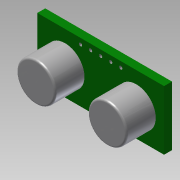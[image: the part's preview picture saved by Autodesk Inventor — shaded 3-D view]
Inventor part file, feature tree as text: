
AUTODESK INVENTOR PART (.ipt)
format: ipt  version: 2015 SP1 (Build 190203100, 203)  size: 141,824 bytes
history: native  units: mm
features: extrude x3, sketch x2, fillet x1, projected_geometry x1
ambient origin geometry x8: Origin, YZ Plane, XZ Plane, XY Plane, X Axis, Y Axis, Z Axis, Center Point
bodies: Solid1 (feature_tree)
feature tree (7):
  extrude  "Extrusion1"  Depth=15.0mm
  sketch  "Sketch2"  dims[d4=2.0mm d5=0.0mm d8=9.8mm d11=32.0mm d12=15.0mm d16=8.0mm d17=9.8mm d19=9.0mm d20=9.0mm d21=7.4mm d22=0.0mm d23=0.5mm d24=0.8mm d25=1.44mm d26=0.8mm d27=2.54mm d28=0.8mm d29=2.54mm d30=7.4mm d31=0.0mm]
  extrude  "Extrusion3"  Depth=7.4mm
  fillet  "Fillet2"  Radius=32.0mm
  extrude  "Extrusion4"  Depth=15.0mm
  sketch  "Sketch1"  dims[d0=32.0mm d1=15.0mm]
  projected_geometry  "Projected Loop1"
